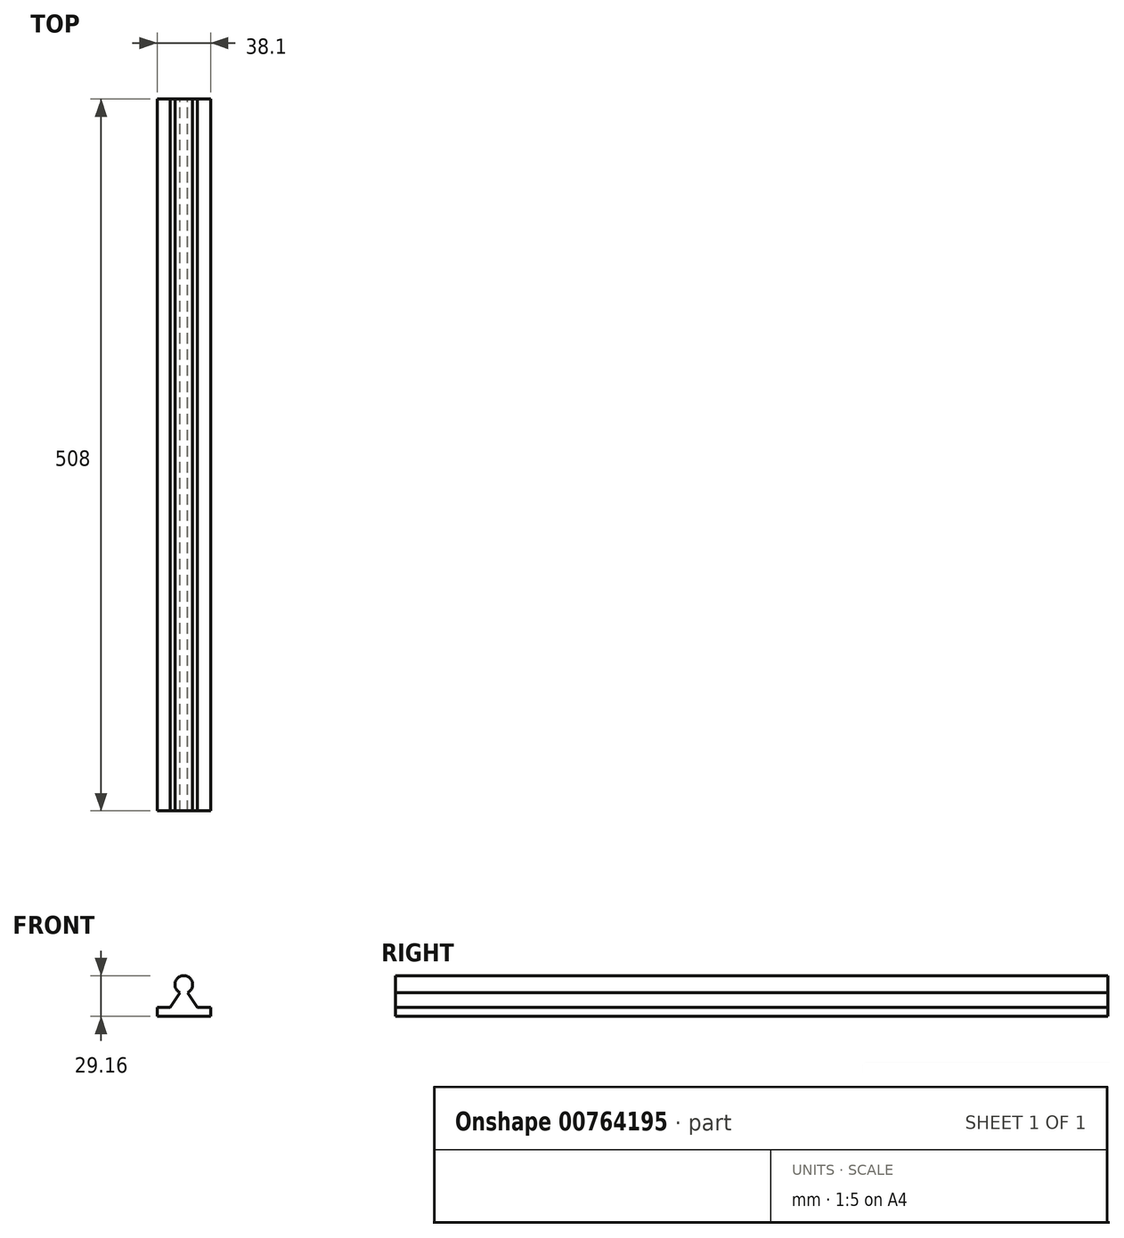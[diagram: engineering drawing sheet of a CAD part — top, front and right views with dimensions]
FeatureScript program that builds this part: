
annotation { "Feature Type Name" : "Feature", "Feature Type Description" : "" }
export const myFeature = defineFeature(function(context is Context, id is Id, definition is map)
    precondition{}
    {
        {
            var Q0;
            Q0=qCreatedBy(makeId("Front.planeOp"),FACE);
            var sketch = newSketch(context, id + "F0", { "sketchPlane" : qUnion([Q0])});
            skCircle(sketch, "E0", {"center": v(-24.28, 9.96) * mm, "radius": 6.35 * mm});
            skLineSegment(sketch, "E1", {"start": v(-24.28, -6.5) * mm, "end": v(-43.33, -6.5) * mm});
            skLineSegment(sketch, "E2", {"start": v(-43.33, -6.5) * mm, "end": v(-43.33, -12.85) * mm});
            skLineSegment(sketch, "E3", {"start": v(-43.33, -12.85) * mm, "end": v(-5.23, -12.85) * mm});
            skLineSegment(sketch, "E4", {"start": v(-5.23, -12.85) * mm, "end": v(-5.23, -6.5) * mm});
            skLineSegment(sketch, "E5", {"start": v(-5.23, -6.5) * mm, "end": v(-24.28, -6.5) * mm});
            skLineSegment(sketch, "E6", {"start": v(-14.75, -6.5) * mm, "end": v(-21.53, 4.24) * mm});
            skLineSegment(sketch, "E7", {"start": v(-33.8, -6.5) * mm, "end": v(-27.03, 4.24) * mm});
            skSolve(sketch);
        }
        {
            var Q0;
            {var subQ0=sQuery(id+"F0.wireOp",EDGE,"E0");var subQ1=makeQuery(id+"F0.imprint","INTERSECT",VERTEX,{"derivedFrom":[subQ0,sQuery(id+"F0.wireOp",EDGE,"E6")]});Q0=makeQuery(id+"F0.imprint","IMPRINT",FACE,{"disambiguationData":[TD([[makeQuery(id+"F0.imprint","IMPRINT",EDGE,{"disambiguationData":[TD([[subQ1,1.0]])],"derivedFrom":subQ0}),1.0]])]});}
            var Q1;
            {var subQ0=sQuery(id+"F0.wireOp",EDGE,"E6");Q1=makeQuery(id+"F0.imprint","IMPRINT",FACE,{"disambiguationData":[TD([[makeQuery(id+"F0.imprint","IMPRINT",EDGE,{"derivedFrom":subQ0}),1.0]])]});}
            var Q2;
            {var subQ0=sQuery(id+"F0.wireOp",EDGE,"E2");Q2=makeQuery(id+"F0.imprint","IMPRINT",FACE,{"disambiguationData":[TD([[makeQuery(id+"F0.imprint","IMPRINT",EDGE,{"derivedFrom":subQ0}),1.0]])]});}
            extrude(context, id + "F1", {"entities" : qUnion([Q0, Q1, Q2]), "depth" : 508 * mm, "offsetDistance" : 25.4 * mm});
        }
    });
